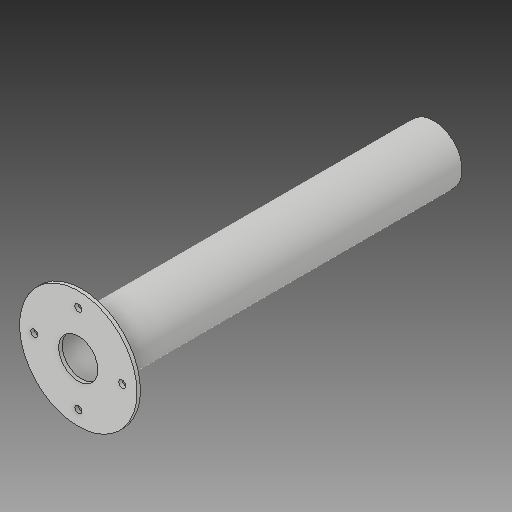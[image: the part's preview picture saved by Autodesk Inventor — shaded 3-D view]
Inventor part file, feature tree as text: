
AUTODESK INVENTOR PART (.ipt)
format: ipt  version: 2017 (Build 210142000, 142)  size: 126,464 bytes
history: native  units: in
note: dims shown in document units (in); Inventor stores cm internally (conversion verified against a paired STEP export)
features: sketch x3, extrude x2, plane x1, hole x1
ambient origin geometry x8: Origin, YZ Plane, XZ Plane, XY Plane, X Axis, Y Axis, Z Axis, Center Point
bodies: Solid1 (feature_tree)
feature tree (7):
  plane  "Work Plane1"
  extrude  "Extrusion1"  Depth=0.1181in TaperAngle=0.0deg
  extrude  "Extrusion2"  Depth=11.811in TaperAngle=0.0deg
  hole  "Hole1"  [1 undecoded]
  sketch  "Sketch2"  dims[d0=1.3189in d2=0.1181in d3=0.0in]
  sketch  "Sketch3"  dims[d4=1.9094in d6=11.811in d7=0.0in]
  sketch  "Sketch4"  dims[d9=2.9528in d10=0.2362in d11=1.5748in d13=360.0deg d15=0.2362in d16=0.75in d17=0.375in d18=0.25in d19=0.5635in d20=1.0in d21=0.8108in d25=3.937in d26=0.0984in]
note: 1 required parameter value undecoded (feature->parameter linkage not recoverable at this tier; creation-order binding heuristic only, values carry confidence <= 0.55)
